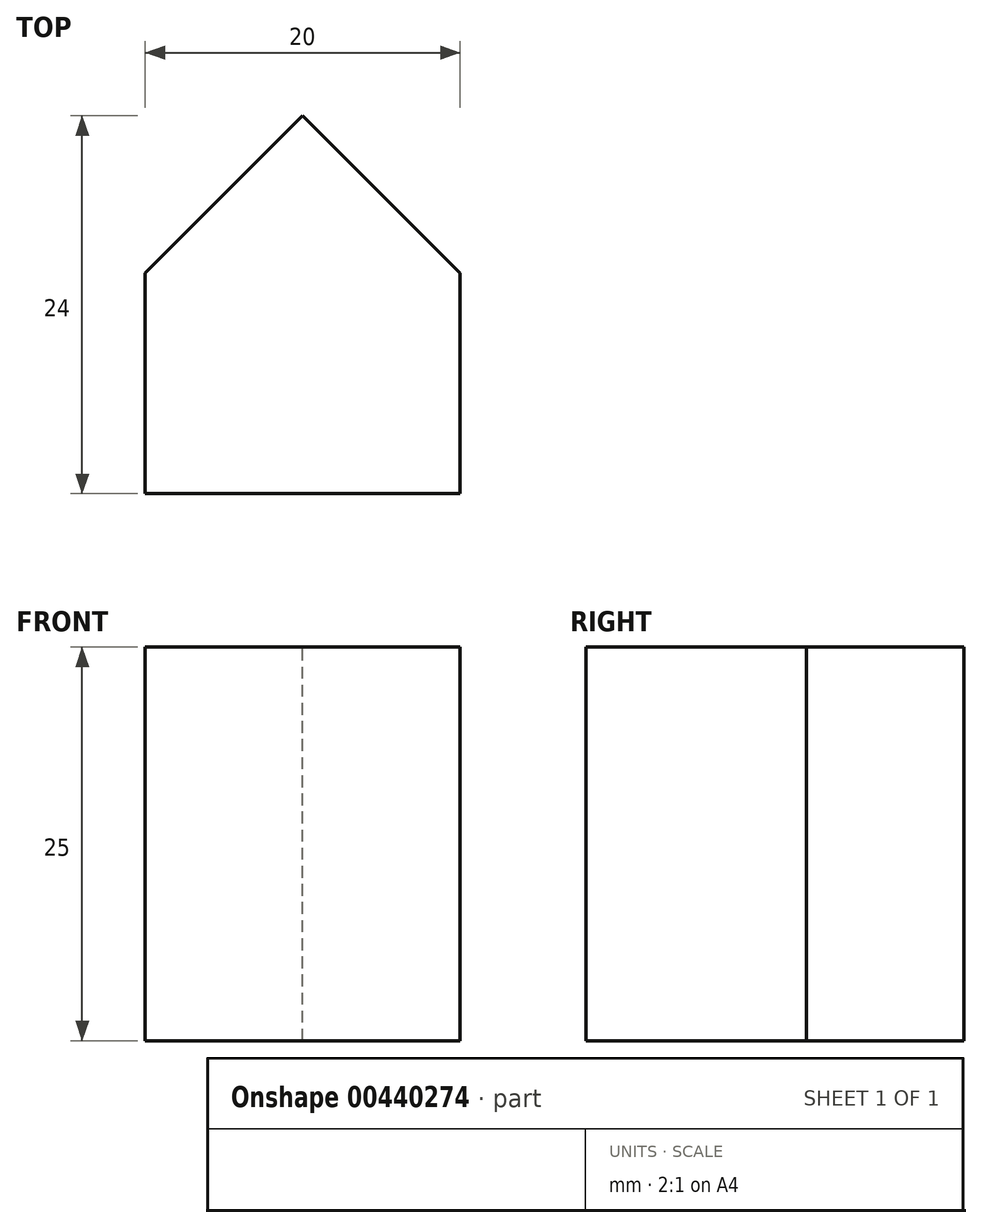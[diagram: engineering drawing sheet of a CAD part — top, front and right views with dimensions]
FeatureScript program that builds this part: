
annotation { "Feature Type Name" : "Feature", "Feature Type Description" : "" }
export const myFeature = defineFeature(function(context is Context, id is Id, definition is map)
    precondition{}
    {
        {
            var Q0;
            Q0=qCreatedBy(makeId("Top.planeOp"),FACE);
            var sketch = newSketch(context, id + "F0", { "sketchPlane" : qUnion([Q0])});
            skLineSegment(sketch, "E0.bottom", {"start": v(-3.58, 19.2) * mm, "end": v(16.42, 19.2) * mm});
            skLineSegment(sketch, "E0.top", {"start": v(-3.58, 5.2) * mm, "end": v(16.42, 5.2) * mm});
            skLineSegment(sketch, "E0.left", {"start": v(-3.58, 19.2) * mm, "end": v(-3.58, 5.2) * mm});
            skLineSegment(sketch, "E0.right", {"start": v(16.42, 19.2) * mm, "end": v(16.42, 5.2) * mm});
            skLineSegment(sketch, "E1", {"start": v(-3.58, 19.2) * mm, "end": v(6.42, 29.2) * mm});
            skLineSegment(sketch, "E2", {"start": v(6.42, 29.2) * mm, "end": v(16.42, 19.2) * mm});
            skLineSegment(sketch, "E3", {"start": v(6.42, 29.2) * mm, "end": v(6.42, 19.2) * mm, "construction": true});
            skSolve(sketch);
        }
        {
            var Q0;
            Q0=makeQuery(id+"F0.imprint","IMPRINT",FACE,{"disambiguationData":[TD([[makeQuery(id+"F0.imprint","IMPRINT",EDGE,{"derivedFrom":sQuery(id+"F0.wireOp",EDGE,"E0.bottom")}),-1.0]])]});
            var Q1;
            Q1=makeQuery(id+"F0.imprint","IMPRINT",FACE,{"disambiguationData":[TD([[makeQuery(id+"F0.imprint","IMPRINT",EDGE,{"derivedFrom":sQuery(id+"F0.wireOp",EDGE,"E0.bottom")}),1.0]])]});
            extrude(context, id + "F1", {"entities" : qUnion([Q0, Q1]), "oppositeDirection" : true, "depth" : 25 * mm});
        }
    });
